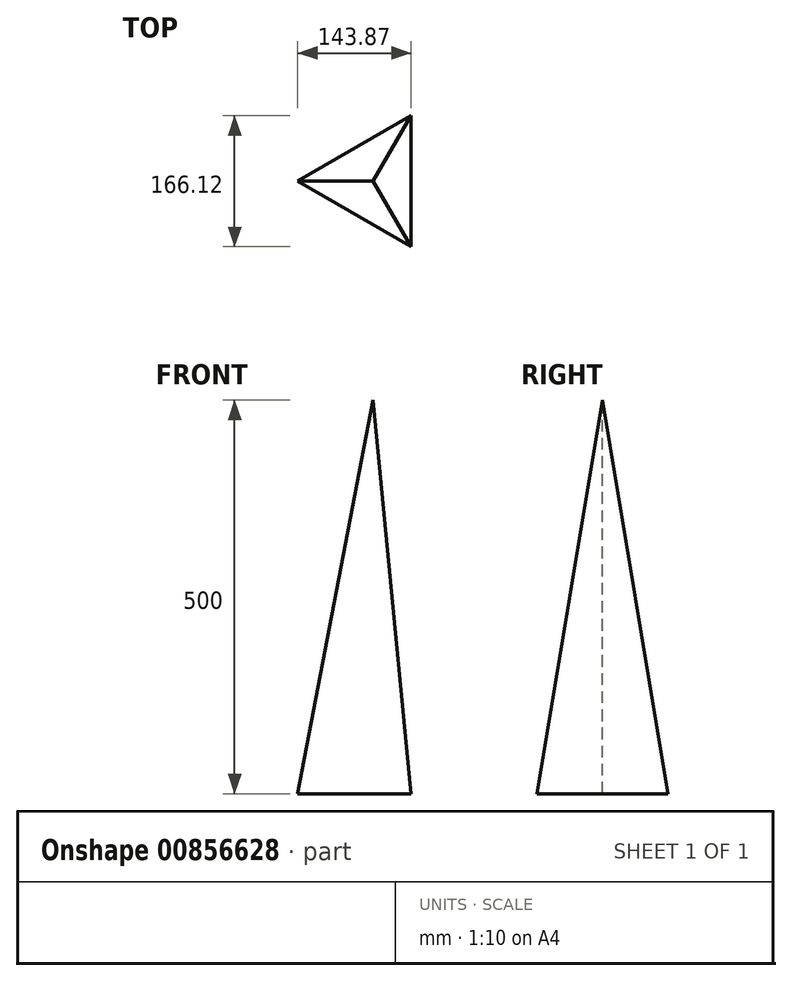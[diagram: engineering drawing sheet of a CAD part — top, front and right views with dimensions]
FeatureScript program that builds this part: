
annotation { "Feature Type Name" : "Feature", "Feature Type Description" : "" }
export const myFeature = defineFeature(function(context is Context, id is Id, definition is map)
    precondition{}
    {
        {
            var Q0;
            Q0=qCreatedBy(makeId("Top.planeOp"),FACE);
            var sketch = newSketch(context, id + "F0", { "sketchPlane" : qUnion([Q0])});
            skCircle(sketch, "E0.cCircle", {"center": v(0, 0) * mm, "radius": 47.96 * mm, "construction": true});
            skLineSegment(sketch, "E0.0", {"start": v(47.96, 83.06) * mm, "end": v(47.96, -83.06) * mm});
            skLineSegment(sketch, "E0.1", {"start": v(47.96, -83.06) * mm, "end": v(-95.91, 0) * mm});
            skLineSegment(sketch, "E0.2", {"start": v(-95.91, 0) * mm, "end": v(47.96, 83.06) * mm});
            skPoint(sketch, "E0.0.midPoint", {"position": v(47.96, 0) * mm});
            skSolve(sketch);
        }
        {
            var Q0;
            Q0=qCreatedBy(makeId("Top.planeOp"),FACE);
            cPlane(context, id + "F1", {"entities" : qUnion([Q0]), "cplaneType" : CPlaneType.OFFSET, "offset" : 500 * mm, "width" : 150 * mm, "height" : 150 * mm});
        }
        {
            var Q0;
            Q0=qCreatedBy(id+"F1.planeOp",FACE);
            var sketch = newSketch(context, id + "F2", { "sketchPlane" : qUnion([Q0])});
            skPoint(sketch, "E1.0", {"position": v(0, 0) * mm});
            skSolve(sketch);
        }
        {
            var Q0;
            Q0=makeQuery(id+"F0.imprint","IMPRINT",FACE,{"disambiguationData":[TD([[makeQuery(id+"F0.imprint","IMPRINT",EDGE,{"derivedFrom":sQuery(id+"F0.wireOp",EDGE,"E0.0")}),-1.0]])]});
            var Q1;
            Q1=sQuery(id+"F2.wireOp",VERTEX,"E1.0");
            loft(context, id + "F3", {"sheetProfilesArray" : [{ "sheetProfileEntities" : qUnion([Q0]) }, { "sheetProfileEntities" : qUnion([Q1]) }]});
        }
    });
